# Revit family: Paper_Holder-Grohe- 40507001
name_source: partatom
category: Specialty Equipment
revit_build: Autodesk Revit 2018 (Build: 20170223_1515(x64)
units: mm (PartAtom-declared; Revit-internal decimal feet)

## family parameters
Cut with Voids When Loaded = No
Host = Face
OmniClass Number = 23.40.20.21.27
OmniClass Title = Towel Bars
Part Type = Normal
Room Calculation Point = No
Round Connector Dimension = Use Diameter
Shared = Yes

## types (1)
- 40507001
    Assembly Code = D2010710
    Body Material = Metal-Grohe-001-Starlight Chrome
    Default Elevation = 0"
    Description = ESSENTIALS CUBE Toilet Paper Holder
    Height = 4"
    Installation Type = Wall Mounted
    Length = 2"
    Manufacturer = Grohe
    Material = Metal-Grohe-001-Starlight Chrome
    Model = 40507001
    Price = Prices may vary. Please consult Manufacturer Representative for most up-to-date price list.
    Product Documentation Link = https://americanstandard.box.com
    Product Page URL = https://www.grohe.us
    Region = North America
    URL = https://www.grohe.us
    Warranty Information = Limited Lifetime Warranty
    Width = 5 1/2"

## geometry (parser evidence)
native form markers: Sweep x3
no freeform markers — native parametric forms only
